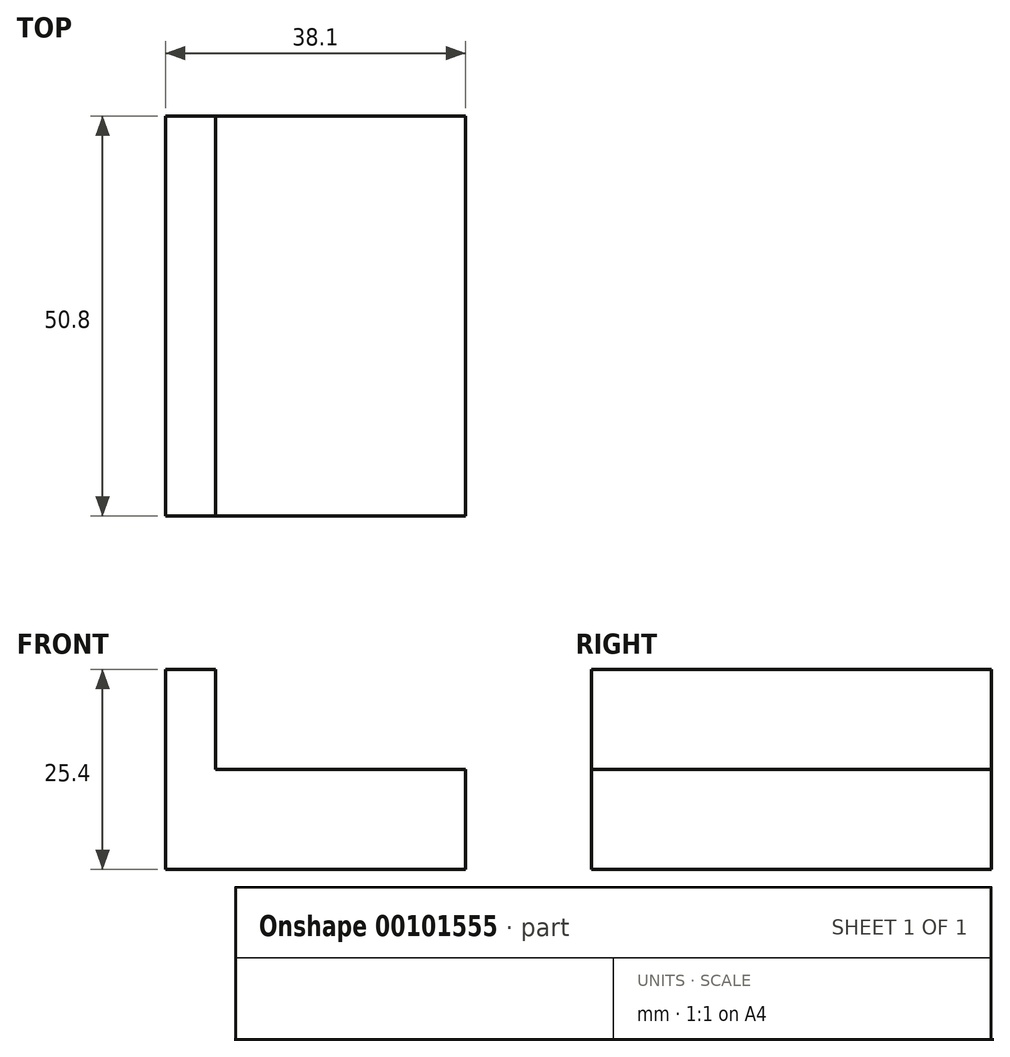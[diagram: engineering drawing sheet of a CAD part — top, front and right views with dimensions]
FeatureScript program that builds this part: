
annotation { "Feature Type Name" : "Feature", "Feature Type Description" : "" }
export const myFeature = defineFeature(function(context is Context, id is Id, definition is map)
    precondition{}
    {
        {
            var Q0;
            Q0=qCreatedBy(makeId("Front.planeOp"),FACE);
            var sketch = newSketch(context, id + "F0", { "sketchPlane" : qUnion([Q0])});
            skLineSegment(sketch, "E0", {"start": v(0, 25.4) * mm, "end": v(0, 0) * mm});
            skLineSegment(sketch, "E1", {"start": v(0, 0) * mm, "end": v(38.1, 0) * mm});
            skLineSegment(sketch, "E2", {"start": v(38.1, 0) * mm, "end": v(38.1, 12.7) * mm});
            skLineSegment(sketch, "E3", {"start": v(38.1, 12.7) * mm, "end": v(6.35, 12.7) * mm});
            skLineSegment(sketch, "E4", {"start": v(6.35, 12.7) * mm, "end": v(6.35, 25.4) * mm});
            skLineSegment(sketch, "E5", {"start": v(6.35, 25.4) * mm, "end": v(0, 25.4) * mm});
            skSolve(sketch);
        }
        {
            var Q0;
            Q0=makeQuery(id+"F0.imprint","IMPRINT",FACE,{"disambiguationData":[TD([[makeQuery(id+"F0.imprint","IMPRINT",EDGE,{"derivedFrom":sQuery(id+"F0.wireOp",EDGE,"E0")}),1.0]])]});
            extrude(context, id + "F1", {"entities" : qUnion([Q0]), "depth" : 50.8 * mm});
        }
    });
